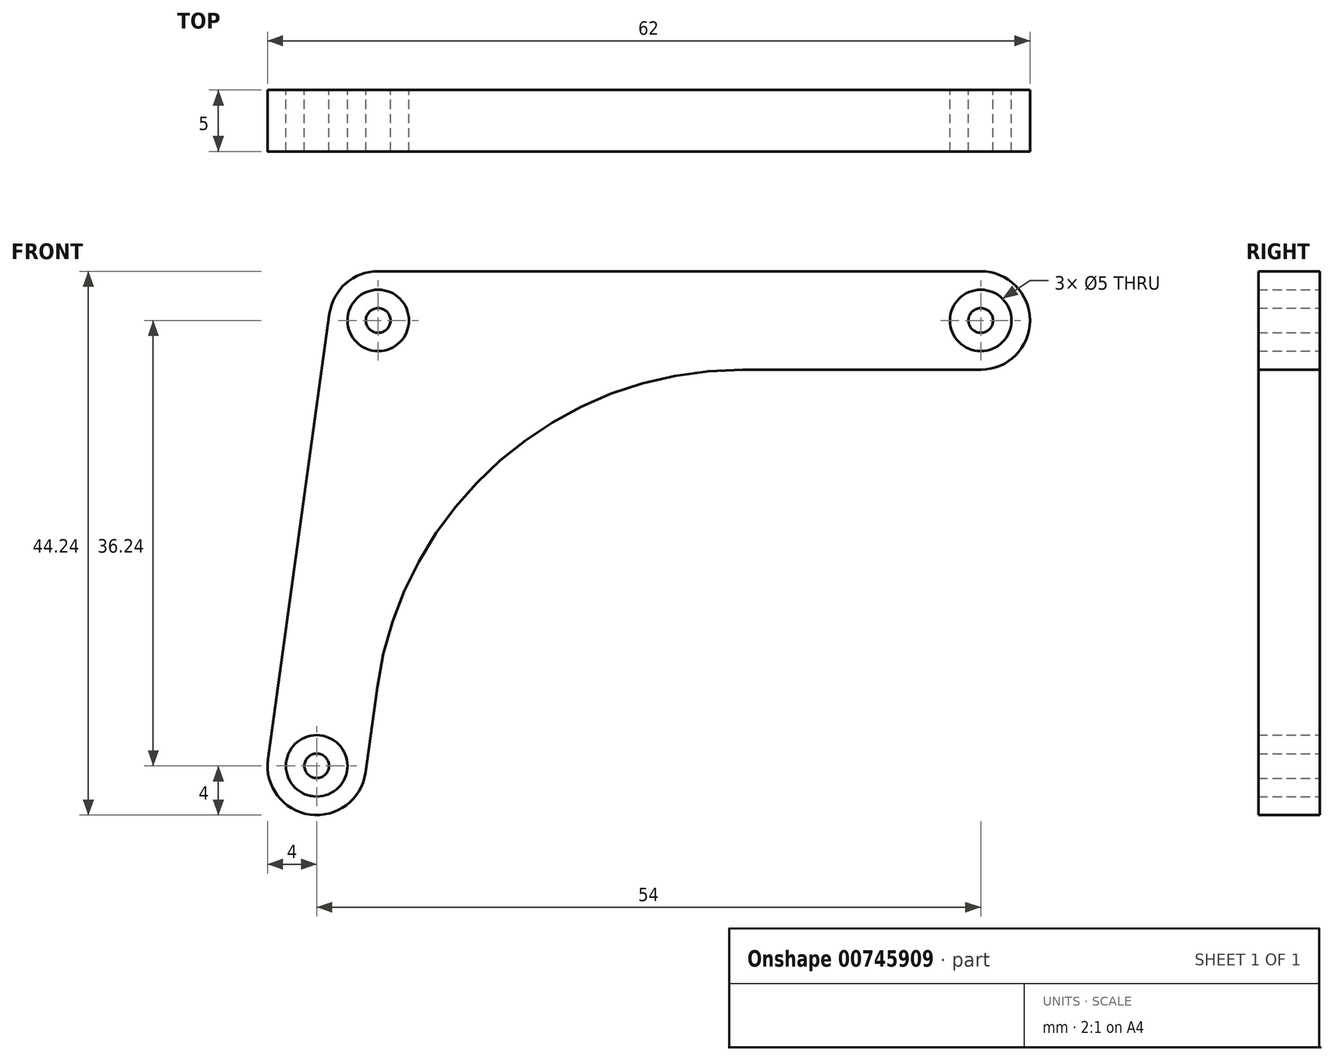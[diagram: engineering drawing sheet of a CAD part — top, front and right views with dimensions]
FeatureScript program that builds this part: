
annotation { "Feature Type Name" : "Feature", "Feature Type Description" : "" }
export const myFeature = defineFeature(function(context is Context, id is Id, definition is map)
    precondition{}
    {
        {
            var Q0;
            Q0=qCreatedBy(makeId("Front.planeOp"),FACE);
            var sketch = newSketch(context, id + "F0", { "sketchPlane" : qUnion([Q0])});
            skCircle(sketch, "E0", {"center": v(0, 0) * mm, "radius": 2.5 * mm});
            skArc(sketch, "E1", {"start": v(0, 4) * mm, "mid": v(-2.63, 3.02) * mm, "end": v(-3.96, 0.55) * mm});
            skCircle(sketch, "E2", {"center": v(0, 0) * mm, "radius": 1 * mm});
            skArc(sketch, "E3", {"start": v(49, -4) * mm, "mid": v(53, 0) * mm, "end": v(49, 4) * mm});
            skCircle(sketch, "E4", {"center": v(49, 0) * mm, "radius": 2.5 * mm});
            skCircle(sketch, "E5", {"center": v(49, 0) * mm, "radius": 1 * mm});
            skLineSegment(sketch, "E6", {"start": v(0, 4) * mm, "end": v(49, 4) * mm});
            skLineSegment(sketch, "E7", {"start": v(29.63, -4) * mm, "end": v(49, -4) * mm});
            skArc(sketch, "E8", {"start": v(-8.96, -35.7) * mm, "mid": v(-5.55, -40.2) * mm, "end": v(-1.04, -36.79) * mm});
            skCircle(sketch, "E9", {"center": v(-5, -36.24) * mm, "radius": 2.5 * mm});
            skCircle(sketch, "E10", {"center": v(-5, -36.24) * mm, "radius": 1 * mm});
            skLineSegment(sketch, "E11", {"start": v(-3.96, 0.55) * mm, "end": v(-8.96, -35.7) * mm});
            skLineSegment(sketch, "E12.0", {"start": v(-0.09, -29.9) * mm, "end": v(-1.04, -36.79) * mm});
            skPoint(sketch, "E13.newPointA", {"position": v(0, -4) * mm});
            skArc(sketch, "E13.filletArc", {"start": v(29.63, -4) * mm, "mid": v(9.92, -11.38) * mm, "end": v(-0.09, -29.9) * mm});
            skSolve(sketch);
        }
        {
            var Q0;
            Q0=makeQuery(id+"F0.imprint","IMPRINT",FACE,{"disambiguationData":[TD([[makeQuery(id+"F0.imprint","IMPRINT",EDGE,{"derivedFrom":sQuery(id+"F0.wireOp",EDGE,"E0")}),-1.0]])]});
            var Q1;
            Q1=makeQuery(id+"F0.imprint","IMPRINT",FACE,{"disambiguationData":[TD([[makeQuery(id+"F0.imprint","IMPRINT",EDGE,{"derivedFrom":sQuery(id+"F0.wireOp",EDGE,"E2")}),1.0]])]});
            var Q2;
            Q2=makeQuery(id+"F0.imprint","IMPRINT",FACE,{"disambiguationData":[TD([[makeQuery(id+"F0.imprint","IMPRINT",EDGE,{"derivedFrom":sQuery(id+"F0.wireOp",EDGE,"E10")}),1.0]])]});
            var Q3;
            Q3=makeQuery(id+"F0.imprint","IMPRINT",FACE,{"disambiguationData":[TD([[makeQuery(id+"F0.imprint","IMPRINT",EDGE,{"derivedFrom":sQuery(id+"F0.wireOp",EDGE,"E5")}),1.0]])]});
            extrude(context, id + "F1", {"entities" : qUnion([Q0, Q1, Q2, Q3]), "depth" : 5 * mm, "offsetDistance" : 25 * mm});
        }
    });
